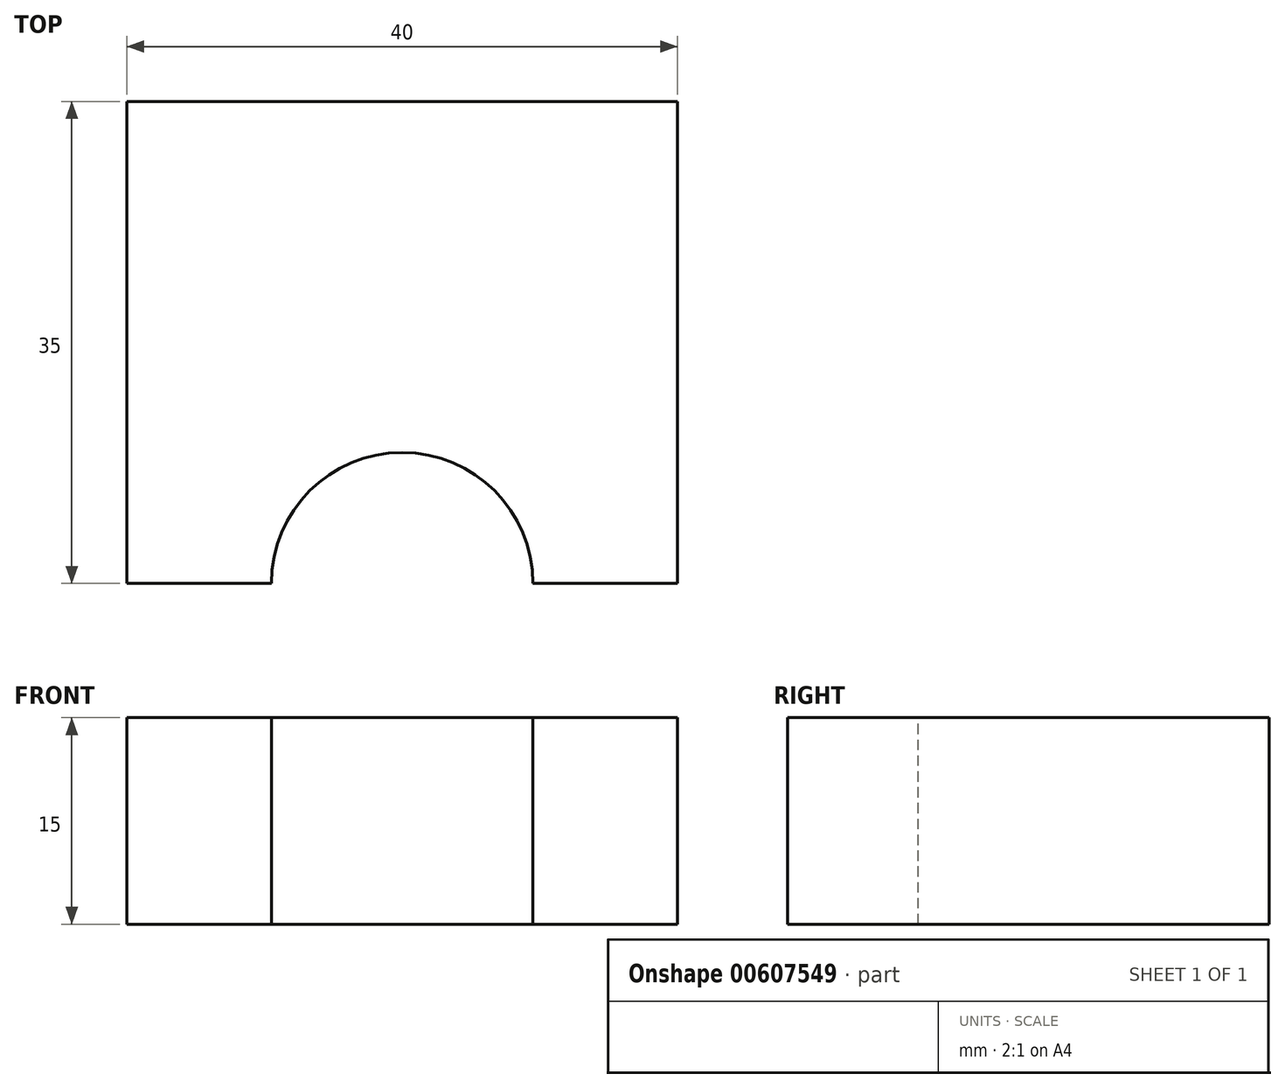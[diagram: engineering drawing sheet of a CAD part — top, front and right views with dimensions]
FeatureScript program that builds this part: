
annotation { "Feature Type Name" : "Feature", "Feature Type Description" : "" }
export const myFeature = defineFeature(function(context is Context, id is Id, definition is map)
    precondition{}
    {
        {
            var Q0;
            Q0=qCreatedBy(makeId("Front.planeOp"),FACE);
            var sketch = newSketch(context, id + "F0", { "sketchPlane" : qUnion([Q0])});
            skLineSegment(sketch, "E0", {"start": v(-20, 0) * mm, "end": v(-20, -15) * mm});
            skLineSegment(sketch, "E1", {"start": v(20, 0) * mm, "end": v(20, -15) * mm});
            skLineSegment(sketch, "E2", {"start": v(-20, -15) * mm, "end": v(20, -15) * mm});
            skLineSegment(sketch, "E3", {"start": v(-20, 0) * mm, "end": v(20, 0) * mm});
            skSolve(sketch);
        }
        {
            var Q0;
            Q0=makeQuery(id+"F0.imprint","IMPRINT",FACE,{"disambiguationData":[TD([[makeQuery(id+"F0.imprint","IMPRINT",EDGE,{"derivedFrom":sQuery(id+"F0.wireOp",EDGE,"E0")}),1.0]])]});
            extrude(context, id + "F1", {"entities" : qUnion([Q0]), "oppositeDirection" : true, "depth" : 35 * mm, "offsetDistance" : 25 * mm});
        }
        {
            var Q0;
            Q0=qCreatedBy(makeId("Top.planeOp"),FACE);
            var sketch = newSketch(context, id + "F2", { "sketchPlane" : qUnion([Q0])});
            skArc(sketch, "E4", {"start": v(9.5, 0) * mm, "mid": v(0, 9.5) * mm, "end": v(-9.5, 0) * mm});
            skSolve(sketch);
        }
        {
            var Q0;
            Q0=sQuery(id+"F2.wireOp",VERTEX,"E4.center");
            var Q1;
            Q1=makeQuery(id+"F1.opExtrude","SWEPT_BODY",BODY,{"disambiguationData":[OSD([sQuery(id+"F0.wireOp",EDGE,"E0"),sQuery(id+"F0.wireOp",EDGE,"E1"),sQuery(id+"F0.wireOp",EDGE,"E2"),sQuery(id+"F0.wireOp",EDGE,"E3")])]});
            hole(context, id + "F3", {"style" : HoleStyle.SIMPLE, "endStyle" : HoleEndStyle.THROUGH, "holeDiameter" : 19 * mm, "majorDiameter" : 5 * mm, "isTappedThrough" : true, "tappedDepth" : 12 * mm, "tapClearance" : 3, "locations" : qUnion([Q0]), "scope" : qUnion([Q1])});
        }
    });
